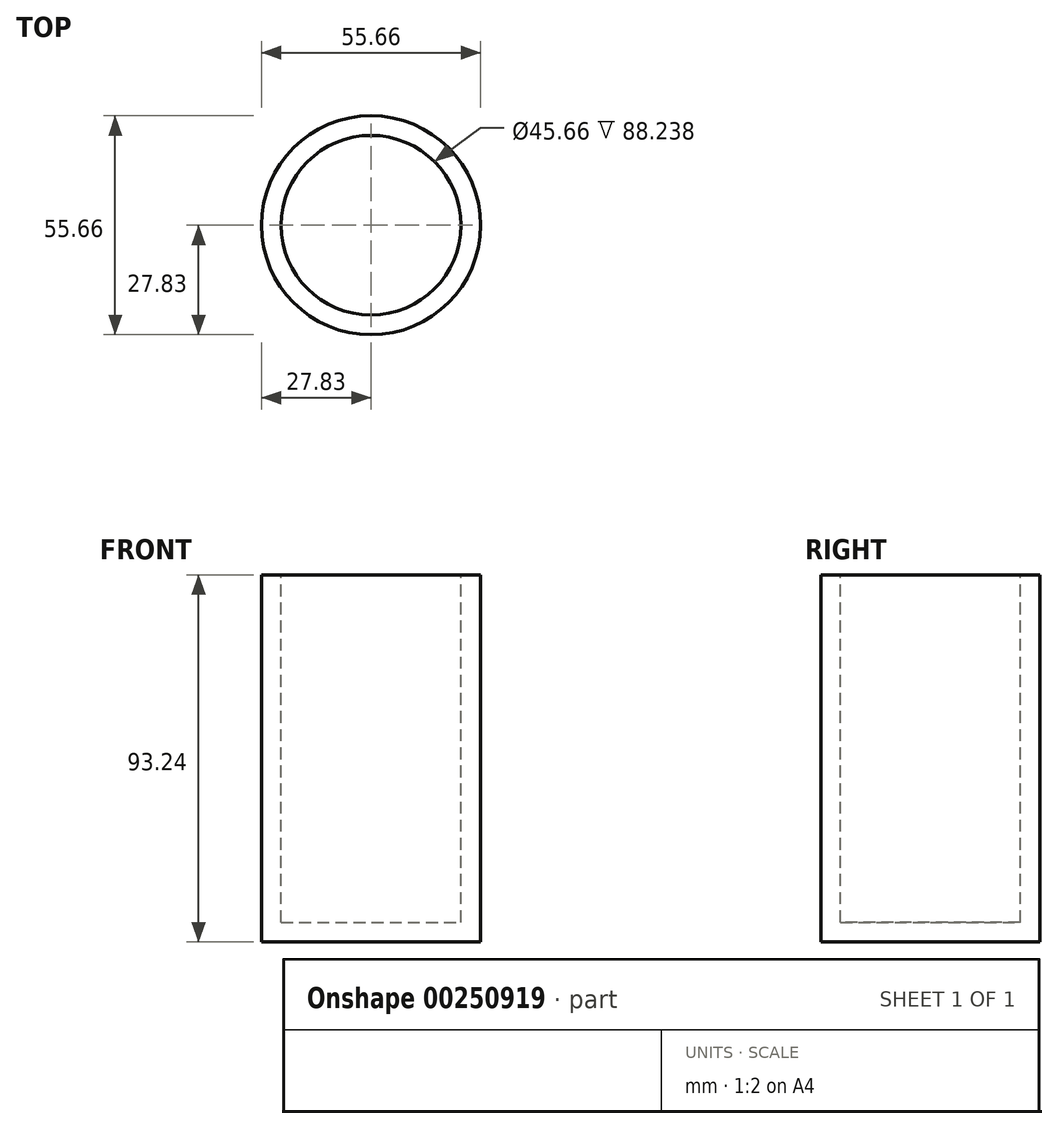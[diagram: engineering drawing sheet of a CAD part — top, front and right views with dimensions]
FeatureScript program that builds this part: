
annotation { "Feature Type Name" : "Feature", "Feature Type Description" : "" }
export const myFeature = defineFeature(function(context is Context, id is Id, definition is map)
    precondition{}
    {
        {
            var Q0;
            Q0=qCreatedBy(makeId("Front.planeOp"),FACE);
            var sketch = newSketch(context, id + "F0", { "sketchPlane" : qUnion([Q0])});
            skLineSegment(sketch, "E0.bottom", {"start": v(-27.83, 46.62) * mm, "end": v(27.83, 46.62) * mm});
            skLineSegment(sketch, "E0.top", {"start": v(-27.83, -46.62) * mm, "end": v(27.83, -46.62) * mm});
            skLineSegment(sketch, "E0.left", {"start": v(-27.83, 46.62) * mm, "end": v(-27.83, -46.62) * mm});
            skLineSegment(sketch, "E0.right", {"start": v(27.83, 46.62) * mm, "end": v(27.83, -46.62) * mm});
            skPoint(sketch, "E0.middle", {"position": v(0, 0) * mm});
            skLineSegment(sketch, "E1", {"start": v(0, 46.62) * mm, "end": v(0, -46.62) * mm});
            skPoint(sketch, "E1.endSnap0", {"position": v(0, -46.62) * mm});
            skSolve(sketch);
        }
        {
            var Q0;
            {var subQ0=sQuery(id+"F0.wireOp",EDGE,"E0.left");Q0=makeQuery(id+"F0.imprint","IMPRINT",FACE,{"disambiguationData":[TD([[makeQuery(id+"F0.imprint","IMPRINT",EDGE,{"derivedFrom":subQ0}),1.0]])]});}
            var Q1;
            Q1=sQuery(id+"F0.wireOp",EDGE,"E1");
            revolve(context, id + "F1", {"entities" : qUnion([Q0]), "axis" : qUnion([Q1]), "revolveType" : RevolveType.FULL});
        }
        {
            var Q0;
            Q0=makeQuery(id+"F1.opRevolve","SWEPT_FACE",FACE,{"disambiguationData":[OSD([sQuery(id+"F0.wireOp",EDGE,"E0.bottom")])]});
            shell(context, id + "F2", {"entities" : qUnion([Q0]), "thickness" : 5 * mm});
        }
    });
